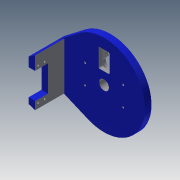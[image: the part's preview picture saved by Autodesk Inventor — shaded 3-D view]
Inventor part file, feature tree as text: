
AUTODESK INVENTOR PART (.ipt)
format: ipt  version: 2013 (Build 170138000, 138)  size: 411,648 bytes
history: native  units: mm
features: sketch x30, extrude x29, fillet x1
ambient origin geometry x8: Origin, YZ Plane, XZ Plane, XY Plane, X Axis, Y Axis, Z Axis, Center Point
bodies: Solid1 (feature_tree)
feature tree (60):
  extrude  "Extrusion1"  Depth=6.0mm
  extrude  "Extrusion2"  Depth=24.3mm
  extrude  "Extrusion3"  Depth=24.3mm
  extrude  "Extrusion4"  Depth=10.0mm
  sketch  "Sketch5"  dims[d9=60.0mm d10=60.0mm]
  extrude  "Extrusion5"  Depth=60.0mm
  extrude  "Extrusion6"  Depth=15.0mm
  extrude  "Extrusion7"  Depth=15.0mm
  extrude  "Extrusion8"  Depth=3.0mm
  extrude  "Extrusion9"  Depth=3.0mm
  extrude  "Extrusion10"  Depth=71.2mm
  extrude  "Extrusion11"  Depth=55.0mm
  extrude  "Extrusion12"  Depth=10.0mm
  extrude  "Extrusion13"  Depth=5.0mm TaperAngle=0.0deg
  extrude  "Extrusion15"  Depth=4.0mm
  extrude  "Extrusion16"  Depth=48.0mm TaperAngle=0.0deg
  extrude  "Extrusion17"  Depth=34.25mm
  extrude  "Extrusion22"  Depth=40.2mm
  sketch  "Sketch24"  dims[d55=49.7mm d56=40.2mm]
  sketch  "Sketch25"  dims[d60=3.0mm d61=3.0mm]
  extrude  "Extrusion23"  Depth=3.0mm
  extrude  "Extrusion24"  Depth=3.0mm
  sketch  "Sketch29"  dims[d64=10.0mm d65=0.0mm d66=3.0mm d67=0.0mm]
  extrude  "Extrusion27"  Depth=3.0mm TaperAngle=0.0deg
  extrude  "Extrusion28"  Depth=4.0mm
  extrude  "Extrusion29"  Depth=8.0mm
  extrude  "Extrusion30"  Depth=15.0mm
  extrude  "Extrusion31"  Depth=6.0mm TaperAngle=0.0deg
  extrude  "Extrusion32"  Depth=14.3mm
  extrude  "Extrusion33"  Depth=48.6mm
  extrude  "Extrusion34"  Depth=35.0mm
  extrude  "Extrusion35"  Depth=35.0mm
  fillet  "Fillet9"  Radius=24.0mm
  extrude  "Extrusion36"  Depth=4.589mm
  sketch  "Sketch1"  dims[d0=120.0mm d1=6.0mm]
  sketch  "Sketch2"  dims[d2=10.0mm d3=0.0mm d4=24.3mm]
  sketch  "Sketch3"  dims[d5=5.0mm d6=24.3mm]
  sketch  "Sketch4"  dims[d7=5.0mm d8=10.0mm]
  sketch  "Sketch6"  dims[d11=15.0mm d12=15.0mm]
  sketch  "Sketch7"  dims[d13=15.0mm d14=15.0mm]
  sketch  "Sketch8"  dims[d15=3.0mm d16=3.0mm]
  sketch  "Sketch9"  dims[d17=3.0mm d18=3.0mm]
  sketch  "Sketch10"  dims[d19=10.0mm d20=0.0mm d31=71.2mm]
  sketch  "Sketch11"  dims[d32=34.25mm d33=55.0mm]
  sketch  "Sketch12"  dims[d34=10.0mm d35=0.0mm d36=10.0mm]
  sketch  "Sketch14"  dims[d37=43.0mm d38=0.0mm d41=5.0mm d42=0.0mm]
  sketch  "Sketch16"  dims[d45=4.0mm d46=4.0mm]
  sketch  "Sketch18"  dims[d47=10.0mm d48=0.0mm d49=48.0mm d50=0.0mm]
  sketch  "Sketch23"  dims[d51=35.0mm d54=34.25mm]
  sketch  "Sketch26"  dims[d62=3.0mm d63=3.0mm]
  sketch  "Sketch30"  dims[d70=14.209mm d71=4.0mm]
  sketch  "Sketch31"  dims[d72=10.0mm d73=0.0mm d74=8.0mm]
  sketch  "Sketch32"  dims[d75=10.0mm d76=0.0mm d78=15.0mm]
  sketch  "Sketch33"  dims[d79=10.0mm d80=6.0mm d81=0.0mm]
  sketch  "Sketch34"  dims[d82=14.3mm d83=14.3mm]
  sketch  "Sketch35"  dims[d84=6.0mm d85=0.0mm d90=48.6mm]
  sketch  "Sketch36"  dims[d91=14.3mm d92=35.0mm]
  sketch  "Sketch37"  dims[d93=14.3mm d94=35.0mm d95=24.0mm d96=0.0mm]
  sketch  "Sketch38"  dims[d97=19.125mm d98=4.589mm]
  sketch  "Sketch39"  dims[d99=10.0mm d100=0.0mm d101=19.125mm d102=4.589mm d103=10.0mm d104=0.0mm d123=15.0mm d124=10.0mm d125=0.0mm d126=35.0mm d129=2.0mm d130=0.0mm d131=10.0mm d132=2.0mm d133=0.0mm d141=63.0mm d142=10.0mm d143=0.0mm d144=7.5mm d145=10.0mm d146=0.0mm d147=3.0mm d148=6.0mm d149=2.0mm d150=10.0mm d151=0.0mm d152=24.0mm d153=0.0mm d154=24.0mm d155=0.0mm d156=6.0mm d157=0.0mm d158=15.0mm d159=24.0mm d160=6.0mm d161=0.0mm d162=16.0mm d163=20.0mm d164=6.0mm d165=0.0mm d166=17.0mm d167=6.0mm d168=0.0mm d169=2.0mm d170=2.0mm d171=0.0mm]
